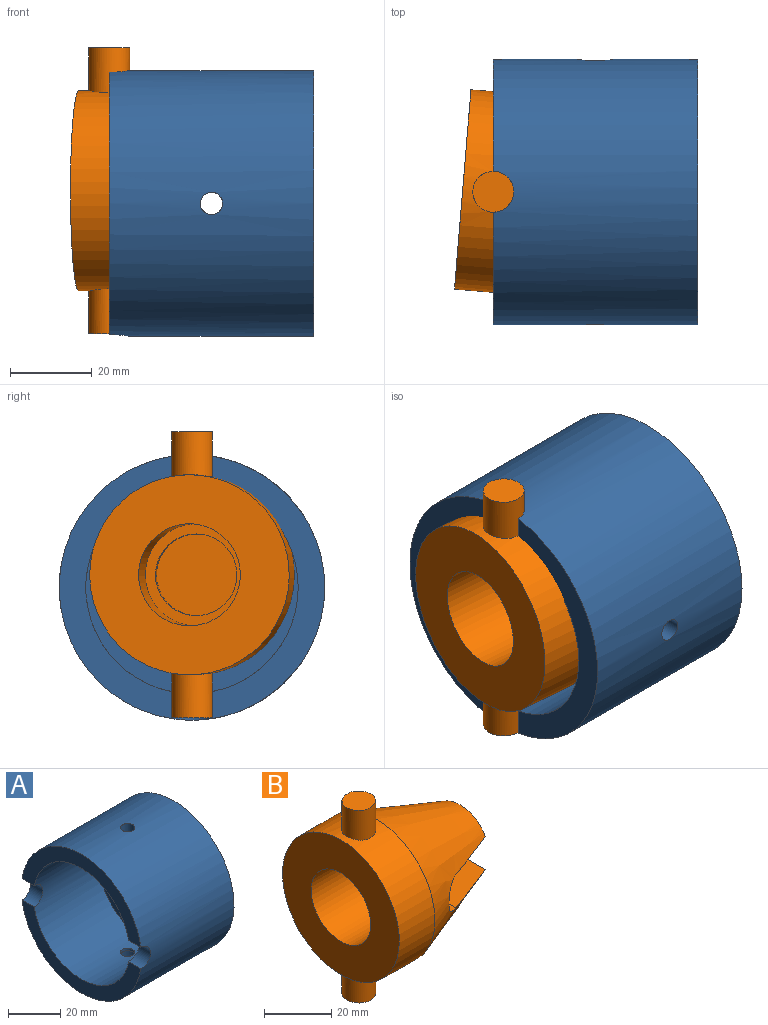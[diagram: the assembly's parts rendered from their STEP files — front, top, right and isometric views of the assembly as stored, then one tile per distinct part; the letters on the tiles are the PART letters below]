
ASSEMBLY  parts=2 mates=1
PART A: 13 faces, bbox 50x65x65 mm
  f0: plane 64.23x27.5mm, normal (-1,0,0), area 532mm2, adj f1,f2,f11,f12
  f1: cylinder r=26mm len=52mm, axis (-1,0,0), area 5591.2mm2, adj f0,f3,f4,f7,f10,f11,f12
  f2: cylinder r=32.5mm len=65mm, axis (-1,0,0), area 10032.4mm2, adj f0,f3,f6,f9,f10,f11,f12
  f3: plane 64.23x27.5mm, normal (-1,0,0), area 532mm2, adj f1,f2,f11,f12
  f4: plane 52x52mm, normal (-1,0,0), area 1809.6mm2, adj f1,f5
  f5: cylinder r=10mm len=20mm, axis (-1,0,0), area 942.5mm2, adj f4,f6
  f6: plane 65x65mm, normal (1,0,0), area 3004.1mm2, adj f2,f5
  f7: cylinder r=2.75mm len=5.5mm, axis (0,0,-1), area 20.8mm2, adj f1,f8
  f8: plane 9.75x9.75mm, normal (0,0,-1), area 50.9mm2, adj f7,f9
  f9: cylinder r=4.88mm len=9.75mm, axis (0,0,-1), area 158.8mm2, adj f2,f8
  f10: cylinder r=2.75mm len=6.65mm, axis (0,0,-1), area 112.6mm2, adj f1,f2
  f11: cylinder r=5mm len=10mm, axis (0,-1,0), area 102.9mm2, adj f0,f1,f2,f3
  f12: cylinder r=5mm len=10mm, axis (0,-1,0), area 102.9mm2, adj f0,f1,f2,f3
PART B: 16 faces, bbox 50.7x49.7x70.7 mm
  f0: plane 21.35x6.24mm, normal (1,0,0), area 94.7mm2, adj f3,f15
  f1: plane 20x20mm, normal (-1,0,0), area 314.2mm2, adj f8
  f2: plane 21.35x6.24mm, normal (1,0,0), area 94.7mm2, adj f3,f13
  f3: cone r=24.5mm half-angle=19.3deg, axis (-1,0,0), area 3615.8mm2, adj f0,f2,f4,f13,f14,f15
  f4: cylinder r=24.5mm len=49mm, axis (-1,0,0), area 2150.9mm2, adj f3,f5,f9,f11
  f5: plane 49x49mm, normal (-1,0,0), area 1394.9mm2, adj f4,f6
  f6: cylinder r=12.5mm len=25mm, axis (-1,0,0), area 1570.8mm2, adj f5,f7
  f7: plane 25x25mm, normal (-1,0,0), area 176.7mm2, adj f6,f8
  f8: cylinder r=10mm len=20mm, axis (-1,0,0), area 188.5mm2, adj f1,f7
  f9: cylinder r=5mm len=11.02mm, axis (0,0,1), area 337.9mm2, adj f4,f10
  f10: plane 10x10mm, normal (0,0,1), area 78.5mm2, adj f9
  f11: cylinder r=5mm len=11.02mm, axis (0,0,1), area 337.9mm2, adj f4,f12
  f12: plane 10x10mm, normal (0,0,-1), area 78.5mm2, adj f11
  f13: plane 37.32x20.74mm, normal (0,0,-1), area 581.3mm2, adj f2,f3,f14
  f14: cylinder r=6mm len=42.7mm, axis (0,-1,0), area 758.9mm2, adj f3,f13,f15
  f15: plane 37.32x20.74mm, normal (0,0,1), area 581.3mm2, adj f0,f3,f14
PLACE A rot(axis=(1,0,0),90deg) t=(92.01,-112,39.38)mm fixed
PLACE B rot(axis=(0,0,-1),4.7deg) t=(154.76,-146.3,42.47)mm
MATE revolute B.f9 <-> A.f11  axis (0,0,1) through (-259.37,-112,71.93)mm
